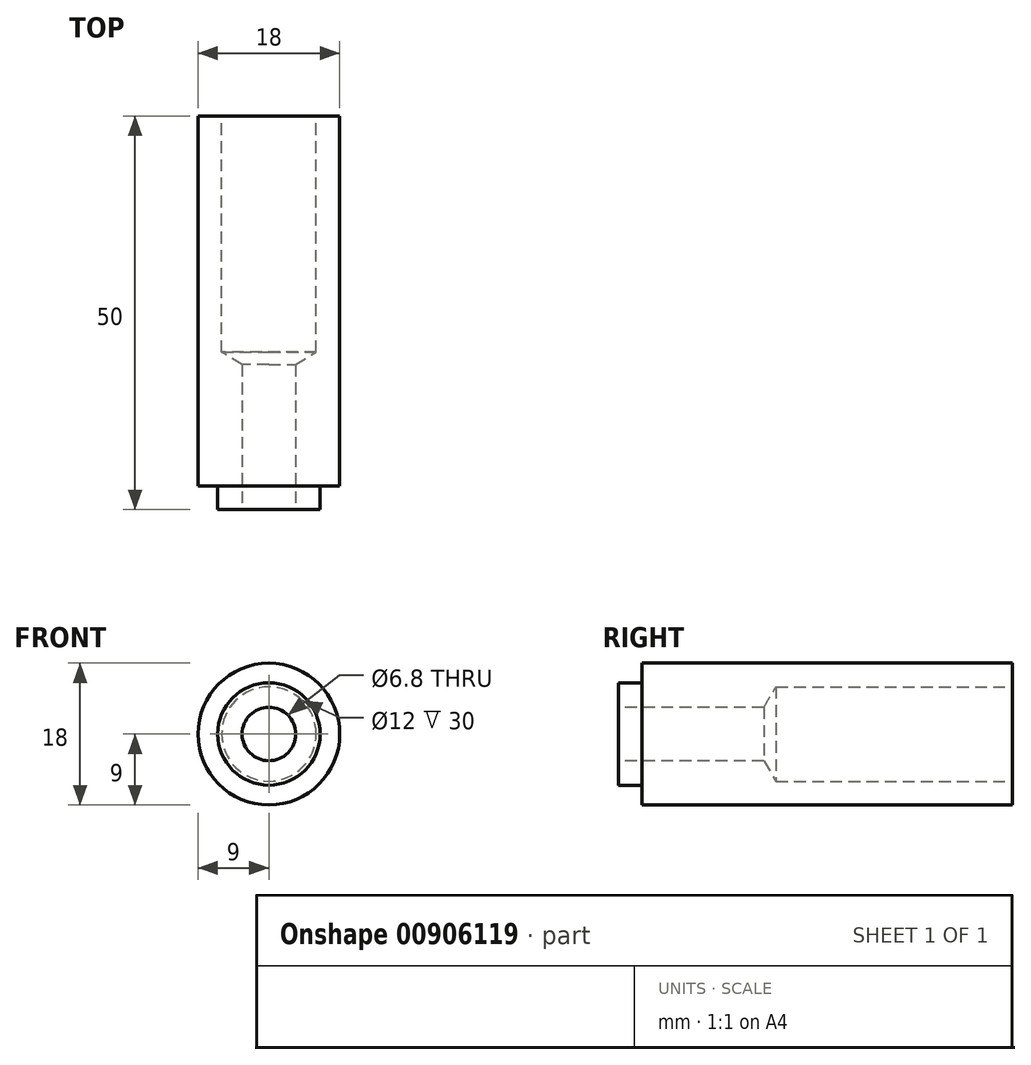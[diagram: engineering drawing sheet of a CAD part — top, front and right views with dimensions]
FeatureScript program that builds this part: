
annotation { "Feature Type Name" : "Feature", "Feature Type Description" : "" }
export const myFeature = defineFeature(function(context is Context, id is Id, definition is map)
    precondition{}
    {
        {
            var Q0;
            Q0=qCreatedBy(makeId("Front.planeOp"),FACE);
            var sketch = newSketch(context, id + "F0", { "sketchPlane" : qUnion([Q0])});
            skCircle(sketch, "E0", {"center": v(0, 0) * mm, "radius": 9 * mm});
            skSolve(sketch);
        }
        {
            var Q0;
            Q0 = qSketchRegion(id + "F0", true);
            extrude(context, id + "F1", {"entities" : qUnion([Q0]), "depth" : 50 * mm, "offsetDistance" : 25 * mm});
        }
        {
            var Q0;
            Q0=makeQuery(id+"F1.opExtrude","CAP_FACE",FACE,{"disambiguationData":[OSD([sQuery(id+"F0.wireOp",EDGE,"E0")])],"isStart":false});
            var sketch = newSketch(context, id + "F2", { "sketchPlane" : qUnion([Q0])});
            skCircle(sketch, "E1", {"center": v(0, 0) * mm, "radius": 6.5 * mm});
            skCircle(sketch, "E2", {"center": v(0, 0) * mm, "radius": 9 * mm});
            skSolve(sketch);
        }
        {
            var Q0;
            Q0 = qSketchRegion(id + "F2", true);
            extrude(context, id + "F3", {"entities" : qUnion([Q0]), "operationType" : NewBodyOperationType.REMOVE, "oppositeDirection" : true, "depth" : 3 * mm, "offsetDistance" : 25 * mm});
        }
        {
            var Q0;
            Q0=makeQuery(id+"F1.opExtrude","CAP_FACE",FACE,{"disambiguationData":[OSD([sQuery(id+"F0.wireOp",EDGE,"E0")])],"isStart":false});
            var sketch = newSketch(context, id + "F4", { "sketchPlane" : qUnion([Q0])});
            skPoint(sketch, "E3", {"position": v(0, 0) * mm});
            skSolve(sketch);
        }
        {
            var Q0;
            Q0=sQuery(id+"F4.wireOp",VERTEX,"E3");
            var Q1;
            Q1=makeQuery(id+"F1.opExtrude","SWEPT_BODY",BODY,{"disambiguationData":[OSD([sQuery(id+"F0.wireOp",EDGE,"E0")])]});
            hole(context, id + "F5", {"style" : HoleStyle.SIMPLE, "endStyle" : HoleEndStyle.BLIND, "standardTappedOrClearance" : lookupTablePath({ "standard" : "ISO", "engagement" : "75%", "pitch" : "1.25 mm", "size" : "M8", "type" : "Tapped" }), "standardBlindInLast" : lookupTablePath({ "standard" : "ISO", "engagement" : "75%", "pitch" : "1.25 mm", "size" : "M8", "type" : "Tapped" }), "holeDiameter" : 6.8 * mm, "majorDiameter" : 8 * mm, "showTappedDepth" : true, "holeDepth" : 20 * mm, "isTappedThrough" : true, "tappedDepth" : 20 * mm, "tapClearance" : 0, "locations" : qUnion([Q0]), "scope" : qUnion([Q1])});
        }
        {
            var Q0;
            Q0=makeQuery(id+"F1.opExtrude","CAP_FACE",FACE,{"disambiguationData":[OSD([sQuery(id+"F0.wireOp",EDGE,"E0")])],"isStart":true});
            var sketch = newSketch(context, id + "F6", { "sketchPlane" : qUnion([Q0])});
            skPoint(sketch, "E4", {"position": v(0, 0) * mm});
            skSolve(sketch);
        }
        {
            var Q0;
            Q0=sQuery(id+"F6.wireOp",VERTEX,"E4");
            var Q1;
            Q1=makeQuery(id+"F1.opExtrude","SWEPT_BODY",BODY,{"disambiguationData":[OSD([sQuery(id+"F0.wireOp",EDGE,"E0")])]});
            hole(context, id + "F7", {"style" : HoleStyle.SIMPLE, "endStyle" : HoleEndStyle.BLIND, "holeDiameter" : 12 * mm, "majorDiameter" : 8 * mm, "holeDepth" : 30 * mm, "isTappedThrough" : true, "tappedDepth" : 16.25 * mm, "tapClearance" : 3, "locations" : qUnion([Q0]), "scope" : qUnion([Q1])});
        }
    });
